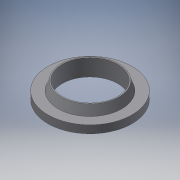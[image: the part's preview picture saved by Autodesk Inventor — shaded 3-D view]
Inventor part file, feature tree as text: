
AUTODESK INVENTOR PART (.ipt)
format: ipt  version: 2017.3 (Build 213257000, 257)  size: 130,560 bytes
history: native  units: in
note: dims shown in document units (in); Inventor stores cm internally (conversion verified against a paired STEP export)
features: revolve x1, sketch x1
ambient origin geometry x8: Origin, YZ Plane, XZ Plane, XY Plane, X Axis, Y Axis, Z Axis, Center Point
bodies: Solid1 (feature_tree)
feature tree (2):
  revolve  "Revolution1"  [1 undecoded]
  sketch  "Sketch1"  dims[d0=13.5in d2=3.75in d3=0.0625in d4=20.375in d5=8.12in d6=15.405in d7=14.0in d8=90.0deg]
note: 1 required parameter value undecoded (feature->parameter linkage not recoverable at this tier; creation-order binding heuristic only, values carry confidence <= 0.55)
